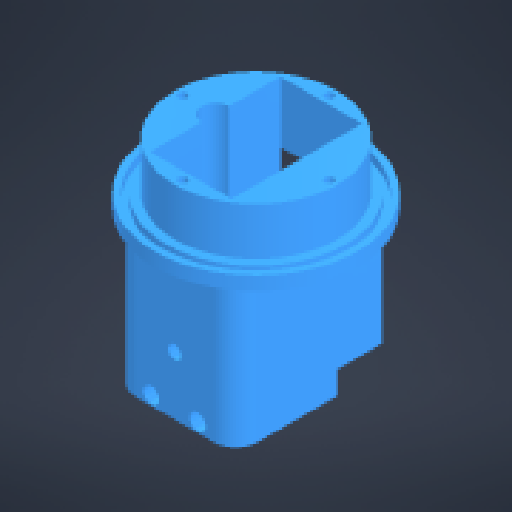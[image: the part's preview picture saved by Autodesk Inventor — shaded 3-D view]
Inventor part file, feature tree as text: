
AUTODESK INVENTOR PART (.ipt)
format: ipt  version: 2024 (Build 280153000, 153)  size: 248,832 bytes
history: native  units: mm
features: reference x10, other x8, extrude x4, sketch x4, fillet x1, imported_body x1
ambient origin geometry x8: Origin, YZ Plane, XZ Plane, XY Plane, X Axis, Y Axis, Z Axis, Center Point
bodies: Body1 (feature_tree)
feature tree (28):
  other  "Твердое тело1"
  extrude  "Выдавливание1"  Depth=3.0mm TaperAngle=0.0deg
  extrude  "Выдавливание2"  Depth=6.25mm TaperAngle=0.0deg
  extrude  "Выдавливание3"  Depth=18.25mm TaperAngle=0.0deg
  other  "РабПлоскость1"
  extrude  "Выдавливание4"  Depth=3.0mm
  fillet  "Сопряжение1"  Radius=37.5mm
  sketch  "Эскиз1"
  reference  "Ссылка1"
  reference  "Ссылка2"
  reference  "Ссылка3"
  sketch  "Эскиз3"
  sketch  "Эскиз4"
  sketch  "Эскиз5"
  reference  "Ссылка4"
  reference  "Ссылка5"
  reference  "Ссылка6"
  reference  "Ссылка7"
  reference  "Ссылка8"
  reference  "Ссылка9"
  reference  "Ссылка10"
  imported_body  "БазТело1"
  parser-record x2  (decoder bookkeeping rows leaked as tree rows — omitted from the tree; the rows remain in map.json)
  other  "bushing_asm.iam"
  other  "ring:1"
  other  "manipulator.iam"
  other  "servo_80kg_base:1"
note: 2 file-system paths scrubbed to <path> (originals preserved in map.json)
